# Revit family: QF_Vollrath_FC-6BG-041T
name_source: partatom
category: Specialty Equipment
revit_build: Autodesk Revit 2018 (Build: 20190510_1515(x64)
units: mm (PartAtom-declared; Revit-internal decimal feet)

## family parameters
Always vertical = Yes
Cut with Voids When Loaded = Yes
Part Type = Normal
Room Calculation Point = No
Round Connector Dimension = Use Diameter
Shared = No
Work Plane-Based = No

## types (4) — shared parameters
Apparent Power = 0 VA
Conn Plug = -
Description = Breath Guard
Elec Conn RI Height = 0"
Foodservice Equipment Identifier = Yes
Manufacturer = Vollrath
zero-valued in all types: Cost, Weight in Pounds

## per-type parameters (varying)
| type | FL Amps | Heat Lamp | Heat and LED Lights | LED Lights | Phase | URL | URL Cutsheet | Volts | Watts |
| FC-6BG-041C | 0 A | No | No | No | 0 |  |  | 0 V | 0 W |
| FC-6BG-041C-LED | 0 A | No | No | Yes | 1 |  |  | 120 V | 15 W |
| FC-6BG-041C-HS | 9 A | Yes | No | No | 1 |  |  | 120 V | 1100 W |
| FC-6BG-041C-HSL | 9 A | No | Yes | No | 1 | www.vollrathfoodservice.com | https://www.vollrathfoodservice.com | 120 V | 1120 W |

note: column(s) folded — value = type name in every type: Model

## geometry (parser evidence)
native form markers: Blend x4, Sweep x11
no freeform markers — native parametric forms only
